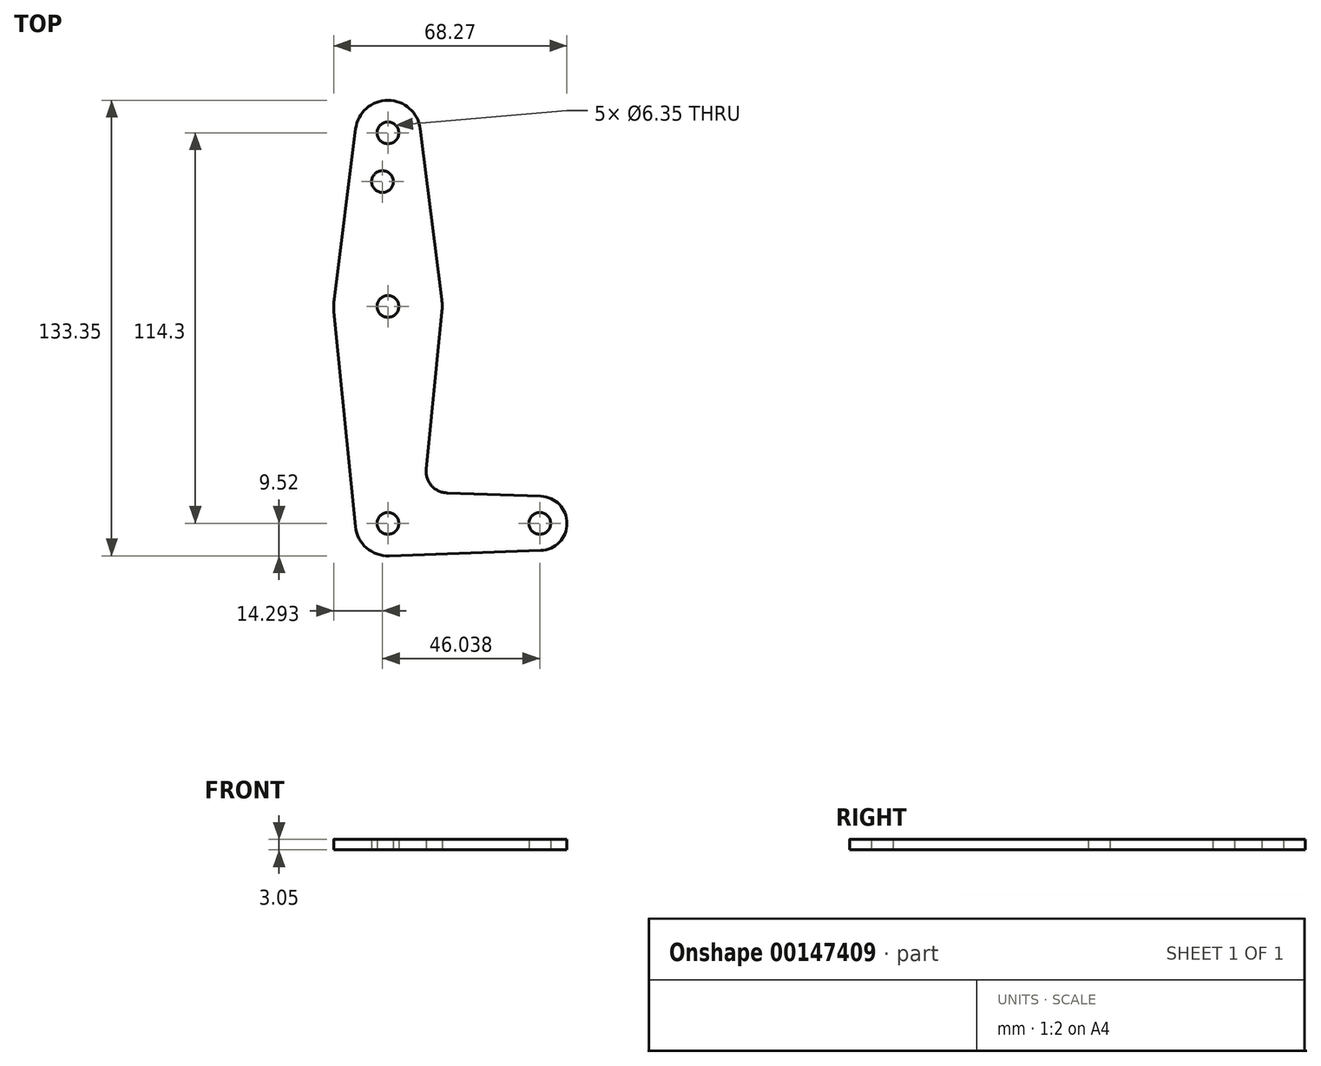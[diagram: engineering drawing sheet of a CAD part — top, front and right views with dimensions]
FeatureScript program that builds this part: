
annotation { "Feature Type Name" : "Feature", "Feature Type Description" : "" }
export const myFeature = defineFeature(function(context is Context, id is Id, definition is map)
    precondition{}
    {
        {
            var Q0;
            Q0=qCreatedBy(makeId("Top.planeOp"),FACE);
            var sketch = newSketch(context, id + "F0", { "sketchPlane" : qUnion([Q0])});
            skLineSegment(sketch, "E0", {"start": v(0, 114.3) * mm, "end": v(0, 0) * mm, "construction": true});
            skLineSegment(sketch, "E1", {"start": v(0, 0) * mm, "end": v(44.45, 0) * mm, "construction": true});
            skCircle(sketch, "E2", {"center": v(0, 114.3) * mm, "radius": 9.53 * mm});
            skCircle(sketch, "E3", {"center": v(0, 63.5) * mm, "radius": 15.88 * mm});
            skCircle(sketch, "E4", {"center": v(0, 0) * mm, "radius": 9.53 * mm});
            skCircle(sketch, "E5", {"center": v(44.45, 0) * mm, "radius": 7.94 * mm});
            skLineSegment(sketch, "E6", {"start": v(-9.45, 115.5) * mm, "end": v(-15.75, 65.48) * mm});
            skLineSegment(sketch, "E7", {"start": v(9.45, 115.5) * mm, "end": v(15.75, 65.48) * mm});
            skLineSegment(sketch, "E8", {"start": v(15.8, 61.91) * mm, "end": v(11.17, 15.9) * mm});
            skLineSegment(sketch, "E9", {"start": v(17.26, 8.91) * mm, "end": v(44.73, 7.93) * mm});
            skLineSegment(sketch, "E10", {"start": v(44.73, -7.93) * mm, "end": v(0.34, -9.52) * mm});
            skCircle(sketch, "E11", {"center": v(0, 114.3) * mm, "radius": 3.17 * mm});
            skCircle(sketch, "E12", {"center": v(0, 63.5) * mm, "radius": 3.18 * mm});
            skCircle(sketch, "E13", {"center": v(0, 0) * mm, "radius": 3.18 * mm});
            skCircle(sketch, "E14", {"center": v(44.45, 0) * mm, "radius": 3.18 * mm});
            skArc(sketch, "E15.filletArc", {"start": v(11.17, 15.9) * mm, "mid": v(12.7, 11.09) * mm, "end": v(17.26, 8.91) * mm});
            skCircle(sketch, "E16", {"center": v(-1.59, 100.03) * mm, "radius": 3.18 * mm});
            skLineSegment(sketch, "E17", {"start": v(-15.8, 61.91) * mm, "end": v(-9.48, -0.95) * mm});
            skSolve(sketch);
        }
        {
            var Q0;
            Q0=makeQuery(id+"F0.imprint","IMPRINT",FACE,{"disambiguationData":[TD([[makeQuery(id+"F0.imprint","IMPRINT",EDGE,{"derivedFrom":sQuery(id+"F0.wireOp",EDGE,"E11")}),-1.0]])]});
            var Q1;
            {var subQ1=sQuery(id+"F0.wireOp",EDGE,"E6");Q1=makeQuery(id+"F0.imprint","IMPRINT",FACE,{"disambiguationData":[TD([[makeQuery(id+"F0.imprint","IMPRINT",EDGE,{"derivedFrom":subQ1}),1.0]])]});}
            var Q2;
            Q2=makeQuery(id+"F0.imprint","IMPRINT",FACE,{"disambiguationData":[TD([[makeQuery(id+"F0.imprint","IMPRINT",EDGE,{"derivedFrom":sQuery(id+"F0.wireOp",EDGE,"E12")}),-1.0]])]});
            var Q3;
            Q3=makeQuery(id+"F0.imprint","IMPRINT",FACE,{"disambiguationData":[TD([[makeQuery(id+"F0.imprint","IMPRINT",EDGE,{"derivedFrom":sQuery(id+"F0.wireOp",EDGE,"E14")}),-1.0]])]});
            var Q4;
            Q4=makeQuery(id+"F0.imprint","IMPRINT",FACE,{"disambiguationData":[TD([[makeQuery(id+"F0.imprint","IMPRINT",EDGE,{"derivedFrom":sQuery(id+"F0.wireOp",EDGE,"E4")}),1.0]])]});
            var Q5;
            {var subQ0=sQuery(id+"F0.wireOp",EDGE,"E8");Q5=makeQuery(id+"F0.imprint","IMPRINT",FACE,{"disambiguationData":[TD([[makeQuery(id+"F0.imprint","IMPRINT",EDGE,{"derivedFrom":subQ0}),-1.0]])]});}
            extrude(context, id + "F1", {"entities" : qUnion([Q0, Q1, Q2, Q3, Q4, Q5]), "depth" : 3.05 * mm});
        }
    });
